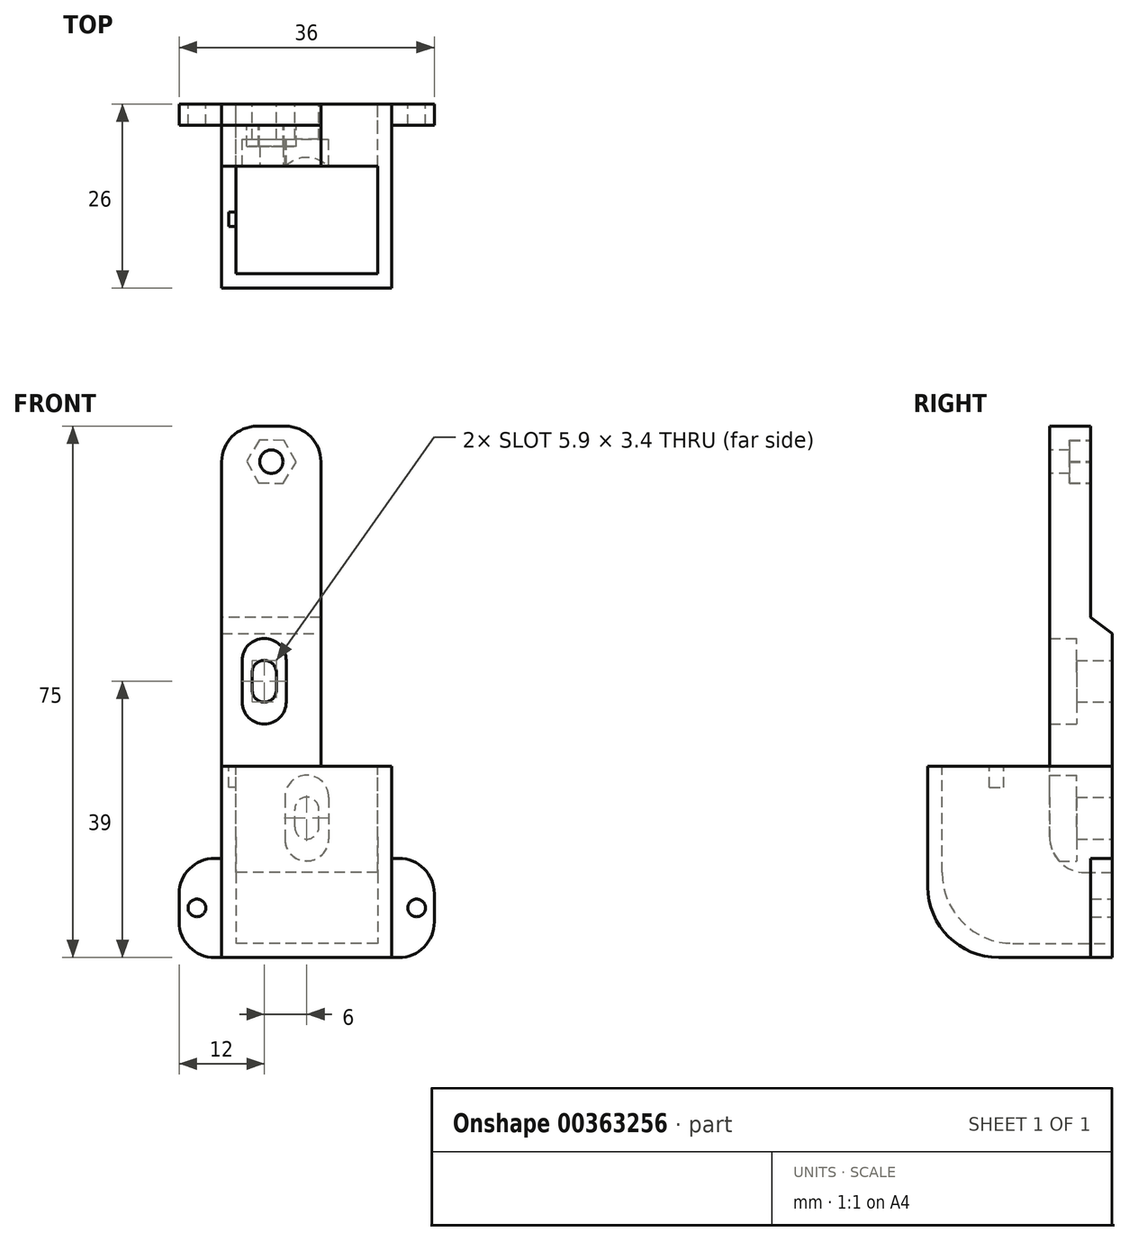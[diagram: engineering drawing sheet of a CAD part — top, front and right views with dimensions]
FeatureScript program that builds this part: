
annotation { "Feature Type Name" : "Feature", "Feature Type Description" : "" }
export const myFeature = defineFeature(function(context is Context, id is Id, definition is map)
    precondition{}
    {
        {
            var Q0;
            Q0=qCreatedBy(makeId("Top.planeOp"),FACE);
            var sketch = newSketch(context, id + "F0", { "sketchPlane" : qUnion([Q0])});
            skLineSegment(sketch, "E0.bottom", {"start": v(12, 13) * mm, "end": v(-12, 13) * mm});
            skLineSegment(sketch, "E0.top", {"start": v(12, -13) * mm, "end": v(-12, -13) * mm});
            skLineSegment(sketch, "E0.left", {"start": v(12, 13) * mm, "end": v(12, -13) * mm});
            skLineSegment(sketch, "E0.right", {"start": v(-12, 13) * mm, "end": v(-12, -13) * mm});
            skPoint(sketch, "E0.middle", {"position": v(0, 0) * mm});
            skSolve(sketch);
        }
        {
            var Q0;
            Q0=qSketchRegion(id+"F0",true);
            extrude(context, id + "F1", {"entities" : qUnion([Q0]), "depth" : 27 * mm});
        }
        {
            var Q0;
            Q0=makeQuery(id+"F1.opExtrude","CAP_FACE",FACE,{"disambiguationData":[OSD([sQuery(id+"F0.wireOp",EDGE,"E0.bottom"),sQuery(id+"F0.wireOp",EDGE,"E0.top"),sQuery(id+"F0.wireOp",EDGE,"E0.left"),sQuery(id+"F0.wireOp",EDGE,"E0.right")])],"isStart":false});
            var sketch = newSketch(context, id + "F2", { "sketchPlane" : qUnion([Q0])});
            skLineSegment(sketch, "E1.bottom", {"start": v(-10, -11) * mm, "end": v(10, -11) * mm});
            skLineSegment(sketch, "E1.top", {"start": v(-10, 4.2) * mm, "end": v(10, 4.2) * mm});
            skLineSegment(sketch, "E1.left", {"start": v(-10, -11) * mm, "end": v(-10, 4.2) * mm});
            skLineSegment(sketch, "E1.right", {"start": v(10, -11) * mm, "end": v(10, 4.2) * mm});
            skSolve(sketch);
        }
        {
            var Q0;
            Q0=qSketchRegion(id+"F2",true);
            extrude(context, id + "F3", {"entities" : qUnion([Q0]), "operationType" : NewBodyOperationType.REMOVE, "oppositeDirection" : true, "depth" : 25 * mm});
        }
        {
            var Q0;
            Q0=makeQuery(id+"F1.opExtrude","SWEPT_FACE",FACE,{"disambiguationData":[OSD([sQuery(id+"F0.wireOp",EDGE,"E0.bottom")])]});
            var sketch = newSketch(context, id + "F4", { "sketchPlane" : qUnion([Q0])});
            skLineSegment(sketch, "E2.bottom", {"start": v(-10, 12) * mm, "end": v(10, 12) * mm});
            skLineSegment(sketch, "E2.top", {"start": v(-10, 2) * mm, "end": v(10, 2) * mm});
            skLineSegment(sketch, "E2.left", {"start": v(-10, 12) * mm, "end": v(-10, 2) * mm});
            skLineSegment(sketch, "E2.right", {"start": v(10, 12) * mm, "end": v(10, 2) * mm});
            skSolve(sketch);
        }
        {
            var Q0;
            Q0=qSketchRegion(id+"F4",true);
            var Q1;
            Q1=makeQuery(id+"F3.boolean.opBoolean","COPY",FACE,{"derivedFrom":makeQuery(id+"F3.opExtrude","SWEPT_FACE",FACE,{"disambiguationData":[OSD([sQuery(id+"F2.wireOp",EDGE,"E1.bottom")])]})});
            extrude(context, id + "F5", {"entities" : qUnion([Q0]), "operationType" : NewBodyOperationType.REMOVE, "endBound" : BoundingType.UP_TO_SURFACE, "oppositeDirection" : true, "endBoundEntityFace" : qUnion([Q1]), "depth" : 25 * mm});
        }
        {
            var Q0;
            Q0=makeQuery(id+"F1.opExtrude","SWEPT_FACE",FACE,{"disambiguationData":[OSD([sQuery(id+"F0.wireOp",EDGE,"E0.right")])]});
            var sketch = newSketch(context, id + "F6", { "sketchPlane" : qUnion([Q0])});
            skLineSegment(sketch, "E3.bottom", {"start": v(-13, 0) * mm, "end": v(-10, 0) * mm});
            skLineSegment(sketch, "E3.top", {"start": v(-13, 14) * mm, "end": v(-10, 14) * mm});
            skLineSegment(sketch, "E3.left", {"start": v(-13, 0) * mm, "end": v(-13, 14) * mm});
            skLineSegment(sketch, "E3.right", {"start": v(-10, 0) * mm, "end": v(-10, 14) * mm});
            skSolve(sketch);
        }
        {
            var Q0;
            Q0=makeQuery(id+"F1.opExtrude","SWEPT_FACE",FACE,{"disambiguationData":[OSD([sQuery(id+"F0.wireOp",EDGE,"E0.left")])]});
            var sketch = newSketch(context, id + "F7", { "sketchPlane" : qUnion([Q0])});
            skLineSegment(sketch, "E4.bottom", {"start": v(13, 0) * mm, "end": v(10, 0) * mm});
            skLineSegment(sketch, "E4.top", {"start": v(13, 14) * mm, "end": v(10, 14) * mm});
            skLineSegment(sketch, "E4.left", {"start": v(13, 0) * mm, "end": v(13, 14) * mm});
            skLineSegment(sketch, "E4.right", {"start": v(10, 0) * mm, "end": v(10, 14) * mm});
            skSolve(sketch);
        }
        {
            var Q0;
            Q0=makeQuery(id+"F7.imprint","IMPRINT",FACE,{"disambiguationData":[TD([[makeQuery(id+"F7.imprint","IMPRINT",EDGE,{"derivedFrom":sQuery(id+"F7.wireOp",EDGE,"E4.bottom")}),-1.0]])]});
            extrude(context, id + "F8", {"entities" : qUnion([Q0]), "operationType" : NewBodyOperationType.ADD, "depth" : 6 * mm});
        }
        {
            var Q0;
            Q0=makeQuery(id+"F6.imprint","IMPRINT",FACE,{"disambiguationData":[TD([[makeQuery(id+"F6.imprint","IMPRINT",EDGE,{"derivedFrom":sQuery(id+"F6.wireOp",EDGE,"E3.bottom")}),1.0]])]});
            extrude(context, id + "F9", {"entities" : qUnion([Q0]), "operationType" : NewBodyOperationType.ADD, "depth" : 6 * mm});
        }
        {
            var Q0;
            Q0=makeQuery(id+"F9.boolean.opBoolean","MERGE",FACE,{"derivedFrom":[makeQuery(id+"F8.boolean.opBoolean","MERGE",FACE,{"derivedFrom":[makeQuery(id+"F1.opExtrude","SWEPT_FACE",FACE,{"disambiguationData":[OSD([sQuery(id+"F0.wireOp",EDGE,"E0.bottom")])]}),makeQuery(id+"F8.opExtrude","SWEPT_FACE",FACE,{"disambiguationData":[OSD([sQuery(id+"F7.wireOp",EDGE,"E4.left")])]})]}),makeQuery(id+"F9.opExtrude","SWEPT_FACE",FACE,{"disambiguationData":[OSD([sQuery(id+"F6.wireOp",EDGE,"E3.left")])]})]});
            var sketch = newSketch(context, id + "F10", { "sketchPlane" : qUnion([Q0])});
            skCircle(sketch, "E5", {"center": v(-15.5, 7) * mm, "radius": 1.25 * mm});
            skCircle(sketch, "E6", {"center": v(15.5, 7) * mm, "radius": 1.25 * mm});
            skSolve(sketch);
        }
        {
            var Q0;
            Q0=qSketchRegion(id+"F10",true);
            extrude(context, id + "F11", {"entities" : qUnion([Q0]), "operationType" : NewBodyOperationType.REMOVE, "endBound" : BoundingType.UP_TO_NEXT, "oppositeDirection" : true, "depth" : 25 * mm});
        }
        {
            var Q0;
            Q0=makeQuery(id+"F8.opExtrude","CAP_EDGE",EDGE,{"disambiguationData":[OSD([sQuery(id+"F7.wireOp",EDGE,"E4.top")])],"isStart":false});
            var Q1;
            Q1=makeQuery(id+"F8.opExtrude","CAP_EDGE",EDGE,{"disambiguationData":[OSD([sQuery(id+"F7.wireOp",EDGE,"E4.bottom")])],"isStart":false});
            var Q2;
            Q2=makeQuery(id+"F9.opExtrude","CAP_EDGE",EDGE,{"disambiguationData":[OSD([sQuery(id+"F6.wireOp",EDGE,"E3.top")])],"isStart":false});
            var Q3;
            Q3=makeQuery(id+"F9.opExtrude","CAP_EDGE",EDGE,{"disambiguationData":[OSD([sQuery(id+"F6.wireOp",EDGE,"E3.bottom")])],"isStart":false});
            fillet(context, id + "F12", {"entities" : qUnion([Q0, Q1, Q2, Q3]), "radius" : 5 * mm, "tangentPropagation" : true, "allowEdgeOverflow" : false});
        }
        {
            var Q0;
            Q0=makeQuery(id+"F1.opExtrude","CAP_FACE",FACE,{"disambiguationData":[OSD([sQuery(id+"F0.wireOp",EDGE,"E0.bottom"),sQuery(id+"F0.wireOp",EDGE,"E0.top"),sQuery(id+"F0.wireOp",EDGE,"E0.left"),sQuery(id+"F0.wireOp",EDGE,"E0.right")])],"isStart":false});
            var sketch = newSketch(context, id + "F13", { "sketchPlane" : qUnion([Q0])});
            skLineSegment(sketch, "E7.bottom", {"start": v(-12, 13) * mm, "end": v(2, 13) * mm});
            skLineSegment(sketch, "E7.top", {"start": v(-12, 4.2) * mm, "end": v(2, 4.2) * mm});
            skLineSegment(sketch, "E7.left", {"start": v(-12, 13) * mm, "end": v(-12, 4.2) * mm});
            skLineSegment(sketch, "E7.right", {"start": v(2, 13) * mm, "end": v(2, 4.2) * mm});
            skSolve(sketch);
        }
        {
            var Q0;
            Q0=makeQuery(id+"F13.imprint","IMPRINT",FACE,{"disambiguationData":[TD([[makeQuery(id+"F13.imprint","IMPRINT",EDGE,{"derivedFrom":sQuery(id+"F13.wireOp",EDGE,"E7.bottom")}),1.0]])]});
            extrude(context, id + "F14", {"entities" : qUnion([Q0]), "operationType" : NewBodyOperationType.ADD, "depth" : 48 * mm});
        }
        {
            var Q0;
            Q0=makeQuery(id+"F14.boolean.opBoolean","MERGE",FACE,{"derivedFrom":[makeQuery(id+"F1.opExtrude","SWEPT_FACE",FACE,{"disambiguationData":[OSD([sQuery(id+"F0.wireOp",EDGE,"E0.right")])]}),makeQuery(id+"F14.opExtrude","SWEPT_FACE",FACE,{"disambiguationData":[OSD([sQuery(id+"F13.wireOp",EDGE,"E7.left")])]})]});
            var sketch = newSketch(context, id + "F15", { "sketchPlane" : qUnion([Q0])});
            skLineSegment(sketch, "E8.bottom", {"start": v(-13, 75) * mm, "end": v(-10, 75) * mm});
            skLineSegment(sketch, "E8.top", {"start": v(-13, 45) * mm, "end": v(-10, 45) * mm});
            skLineSegment(sketch, "E8.left", {"start": v(-13, 75) * mm, "end": v(-13, 45) * mm});
            skLineSegment(sketch, "E8.right", {"start": v(-10, 75) * mm, "end": v(-10, 45) * mm});
            skLineSegment(sketch, "E9", {"start": v(-13, 18) * mm, "end": v(-7.21, 18) * mm, "construction": true});
            skSolve(sketch);
        }
        {
            var Q0;
            Q0=qSketchRegion(id+"F15",true);
            extrude(context, id + "F16", {"entities" : qUnion([Q0]), "operationType" : NewBodyOperationType.REMOVE, "endBound" : BoundingType.UP_TO_NEXT, "oppositeDirection" : true, "depth" : 25 * mm});
        }
        {
            var Q0;
            Q0=makeQuery(id+"F16.boolean.opBoolean","COPY",EDGE,{"derivedFrom":makeQuery(id+"F16.opExtrude","SWEPT_EDGE",EDGE,{"disambiguationData":[OSD([sQuery(id+"F15.wireOp",EDGE,"E8.top"),sQuery(id+"F15.wireOp",EDGE,"E8.right")])]})});
            chamfer(context, id + "F17", {"entities" : qUnion([Q0]), "chamferType" : ChamferType.TWO_OFFSETS, "width1" : 3 * mm, "oppositeDirection" : false, "width2" : 4 * mm, "tangentPropagation" : true});
        }
        {
            var Q0;
            Q0=makeQuery(id+"F14.boolean.opBoolean","MERGE",FACE,{"derivedFrom":[makeQuery(id+"F3.boolean.opBoolean","COPY",FACE,{"derivedFrom":makeQuery(id+"F3.opExtrude","SWEPT_FACE",FACE,{"disambiguationData":[OSD([sQuery(id+"F2.wireOp",EDGE,"E1.top")])]})}),makeQuery(id+"F14.opExtrude","SWEPT_FACE",FACE,{"disambiguationData":[OSD([sQuery(id+"F13.wireOp",EDGE,"E7.top")])]})]});
            var sketch = newSketch(context, id + "F18", { "sketchPlane" : qUnion([Q0])});
            skCircle(sketch, "E10", {"center": v(-5, 70) * mm, "radius": 1.65 * mm});
            skSolve(sketch);
        }
        {
            var Q0;
            Q0=qSketchRegion(id+"F18",true);
            extrude(context, id + "F19", {"entities" : qUnion([Q0]), "operationType" : NewBodyOperationType.REMOVE, "endBound" : BoundingType.UP_TO_NEXT, "oppositeDirection" : true, "depth" : 25 * mm});
        }
        {
            var Q0;
            Q0=makeQuery(id+"F16.boolean.opBoolean","COPY",FACE,{"derivedFrom":makeQuery(id+"F16.opExtrude","SWEPT_FACE",FACE,{"disambiguationData":[OSD([sQuery(id+"F15.wireOp",EDGE,"E8.right")])]})});
            var sketch = newSketch(context, id + "F20", { "sketchPlane" : qUnion([Q0])});
            skCircle(sketch, "E11.cCircle", {"center": v(5, 70) * mm, "radius": 3.5 * mm, "construction": true});
            skLineSegment(sketch, "E11.0", {"start": v(6.7, 73.06) * mm, "end": v(8.5, 70.06) * mm});
            skLineSegment(sketch, "E11.1", {"start": v(8.5, 70.06) * mm, "end": v(6.8, 67) * mm});
            skLineSegment(sketch, "E11.2", {"start": v(6.8, 67) * mm, "end": v(3.3, 66.94) * mm});
            skLineSegment(sketch, "E11.3", {"start": v(3.3, 66.94) * mm, "end": v(1.5, 69.94) * mm});
            skLineSegment(sketch, "E11.4", {"start": v(1.5, 69.94) * mm, "end": v(3.2, 73) * mm});
            skLineSegment(sketch, "E11.5", {"start": v(3.2, 73) * mm, "end": v(6.7, 73.06) * mm});
            skSolve(sketch);
        }
        {
            var Q0;
            Q0=qSketchRegion(id+"F20",true);
            extrude(context, id + "F21", {"entities" : qUnion([Q0]), "operationType" : NewBodyOperationType.REMOVE, "oppositeDirection" : true, "depth" : 3 * mm});
        }
        {
            var Q0;
            Q0=makeQuery(id+"F14.boolean.opBoolean","MERGE",FACE,{"derivedFrom":[makeQuery(id+"F9.boolean.opBoolean","MERGE",FACE,{"derivedFrom":[makeQuery(id+"F8.boolean.opBoolean","MERGE",FACE,{"derivedFrom":[makeQuery(id+"F1.opExtrude","SWEPT_FACE",FACE,{"disambiguationData":[OSD([sQuery(id+"F0.wireOp",EDGE,"E0.bottom")])]}),makeQuery(id+"F8.opExtrude","SWEPT_FACE",FACE,{"disambiguationData":[OSD([sQuery(id+"F7.wireOp",EDGE,"E4.left")])]})]}),makeQuery(id+"F9.opExtrude","SWEPT_FACE",FACE,{"disambiguationData":[OSD([sQuery(id+"F6.wireOp",EDGE,"E3.left")])]})]}),makeQuery(id+"F14.opExtrude","SWEPT_FACE",FACE,{"disambiguationData":[OSD([sQuery(id+"F13.wireOp",EDGE,"E7.bottom")])]})]});
            var sketch = newSketch(context, id + "F22", { "sketchPlane" : qUnion([Q0])});
            skLineSegment(sketch, "E12", {"start": v(-12, 18) * mm, "end": v(12, 18) * mm, "construction": true});
            skLineSegment(sketch, "E13", {"start": v(0, 18) * mm, "end": v(0, 19.67) * mm, "construction": true});
            skLineSegment(sketch, "E14", {"start": v(0, 18.42) * mm, "end": v(0, 20.93) * mm, "construction": true});
            skPoint(sketch, "E15", {"position": v(0, 19.67) * mm});
            skArc(sketch, "E16.0.startCap", {"start": v(1.7, 18.42) * mm, "mid": v(0, 16.72) * mm, "end": v(-1.7, 18.42) * mm});
            skArc(sketch, "E16.0.endCap", {"start": v(-1.7, 20.92) * mm, "mid": v(0, 22.62) * mm, "end": v(1.7, 20.92) * mm});
            skLineSegment(sketch, "E16.0.left", {"start": v(-1.7, 18.42) * mm, "end": v(-1.7, 20.92) * mm});
            skLineSegment(sketch, "E16.0.right", {"start": v(1.7, 18.42) * mm, "end": v(1.7, 20.92) * mm});
            skLineSegment(sketch, "E17", {"start": v(0, 22.62) * mm, "end": v(0, 16.72) * mm});
            skArc(sketch, "E18.0.startCap", {"start": v(-3.1, 22.62) * mm, "mid": v(0, 25.72) * mm, "end": v(3.1, 22.62) * mm});
            skArc(sketch, "E18.0.endCap", {"start": v(3.1, 16.72) * mm, "mid": v(0, 13.62) * mm, "end": v(-3.1, 16.72) * mm});
            skLineSegment(sketch, "E18.0.left", {"start": v(3.1, 22.62) * mm, "end": v(3.1, 16.72) * mm});
            skLineSegment(sketch, "E18.0.right", {"start": v(-3.1, 22.62) * mm, "end": v(-3.1, 16.72) * mm});
            skLineSegment(sketch, "E19", {"start": v(6, 40.25) * mm, "end": v(6, 37.75) * mm});
            skPoint(sketch, "E20", {"position": v(6, 39) * mm});
            skArc(sketch, "E21.0.startCap", {"start": v(4.3, 40.25) * mm, "mid": v(6, 41.95) * mm, "end": v(7.7, 40.25) * mm});
            skArc(sketch, "E21.0.endCap", {"start": v(7.7, 37.75) * mm, "mid": v(6, 36.05) * mm, "end": v(4.3, 37.75) * mm});
            skLineSegment(sketch, "E21.0.left", {"start": v(7.7, 40.25) * mm, "end": v(7.7, 37.75) * mm});
            skLineSegment(sketch, "E21.0.right", {"start": v(4.3, 40.25) * mm, "end": v(4.3, 37.75) * mm});
            skLineSegment(sketch, "E22", {"start": v(6, 41.95) * mm, "end": v(6, 36.05) * mm});
            skArc(sketch, "E23.0.startCap", {"start": v(2.9, 41.95) * mm, "mid": v(6, 45.05) * mm, "end": v(9.1, 41.95) * mm});
            skArc(sketch, "E23.0.endCap", {"start": v(9.1, 36.05) * mm, "mid": v(6, 32.95) * mm, "end": v(2.9, 36.05) * mm});
            skLineSegment(sketch, "E23.0.left", {"start": v(9.1, 41.95) * mm, "end": v(9.1, 36.05) * mm});
            skLineSegment(sketch, "E23.0.right", {"start": v(2.9, 41.95) * mm, "end": v(2.9, 36.05) * mm});
            skSolve(sketch);
        }
        {
            var Q0;
            Q0=qSketchRegion(id+"F22",true);
            var Q1;
            {var subQ0=sQuery(id+"F22.wireOp",EDGE,"E16.0.left");Q1=makeQuery(id+"F22.imprint","IMPRINT",FACE,{"disambiguationData":[TD([[makeQuery(id+"F22.imprint","IMPRINT",EDGE,{"derivedFrom":subQ0}),-1.0]])]});}
            var Q2;
            {var subQ0=sQuery(id+"F22.wireOp",EDGE,"E16.0.right");Q2=makeQuery(id+"F22.imprint","IMPRINT",FACE,{"disambiguationData":[TD([[makeQuery(id+"F22.imprint","IMPRINT",EDGE,{"derivedFrom":subQ0}),1.0]])]});}
            var Q3;
            {var subQ0=sQuery(id+"F22.wireOp",EDGE,"E21.0.left");Q3=makeQuery(id+"F22.imprint","IMPRINT",FACE,{"disambiguationData":[TD([[makeQuery(id+"F22.imprint","IMPRINT",EDGE,{"derivedFrom":subQ0}),-1.0]])]});}
            var Q4;
            {var subQ4=sQuery(id+"F22.wireOp",EDGE,"E21.0.right");Q4=makeQuery(id+"F22.imprint","IMPRINT",FACE,{"disambiguationData":[TD([[makeQuery(id+"F22.imprint","IMPRINT",EDGE,{"derivedFrom":subQ4}),1.0]])]});}
            extrude(context, id + "F23", {"entities" : qUnion([Q0, Q1, Q2, Q3, Q4]), "operationType" : NewBodyOperationType.REMOVE, "endBound" : BoundingType.UP_TO_NEXT, "oppositeDirection" : true, "depth" : 25 * mm});
        }
        {
            var Q0;
            Q0=qSketchRegion(id+"F22",true);
            extrude(context, id + "F24", {"entities" : qUnion([Q0]), "operationType" : NewBodyOperationType.ADD, "oppositeDirection" : true, "depth" : 5 * mm});
        }
        {
            var Q0;
            Q0=makeQuery(id+"F1.opExtrude","CAP_EDGE",EDGE,{"disambiguationData":[OSD([sQuery(id+"F0.wireOp",EDGE,"E0.top")])],"isStart":true});
            var Q1;
            Q1=makeQuery(id+"F3.boolean.opBoolean","COPY",EDGE,{"derivedFrom":makeQuery(id+"F3.opExtrude","CAP_EDGE",EDGE,{"disambiguationData":[OSD([sQuery(id+"F2.wireOp",EDGE,"E1.bottom")])],"isStart":false})});
            fillet(context, id + "F25", {"entities" : qUnion([Q0, Q1]), "radius" : 10 * mm, "tangentPropagation" : true, "allowEdgeOverflow" : false});
        }
        {
            var Q0;
            Q0=makeQuery(id+"F5.boolean.opBoolean","INTERSECT",EDGE,{"derivedFrom":[makeQuery(id+"F3.boolean.opBoolean","COPY",FACE,{"derivedFrom":makeQuery(id+"F3.opExtrude","SWEPT_FACE",FACE,{"disambiguationData":[OSD([sQuery(id+"F2.wireOp",EDGE,"E1.top")])]})}),makeQuery(id+"F5.opExtrude","SWEPT_FACE",FACE,{"disambiguationData":[OSD([sQuery(id+"F4.wireOp",EDGE,"E2.bottom")])]})]});
            fillet(context, id + "F26", {"entities" : qUnion([Q0]), "radius" : 5 * mm, "tangentPropagation" : true, "allowEdgeOverflow" : false});
        }
        {
            var Q0;
            Q0=makeQuery(id+"F1.opExtrude","CAP_FACE",FACE,{"disambiguationData":[OSD([sQuery(id+"F0.wireOp",EDGE,"E0.bottom"),sQuery(id+"F0.wireOp",EDGE,"E0.top"),sQuery(id+"F0.wireOp",EDGE,"E0.left"),sQuery(id+"F0.wireOp",EDGE,"E0.right")])],"isStart":false});
            var sketch = newSketch(context, id + "F27", { "sketchPlane" : qUnion([Q0])});
            skLineSegment(sketch, "E24.bottom", {"start": v(-10, -4.3) * mm, "end": v(-11, -4.3) * mm});
            skLineSegment(sketch, "E24.top", {"start": v(-10, -2.3) * mm, "end": v(-11, -2.3) * mm});
            skLineSegment(sketch, "E24.left", {"start": v(-10, -4.3) * mm, "end": v(-10, -2.3) * mm});
            skLineSegment(sketch, "E24.right", {"start": v(-11, -4.3) * mm, "end": v(-11, -2.3) * mm});
            skSolve(sketch);
        }
        {
            var Q0;
            Q0=makeQuery(id+"F27.imprint","IMPRINT",FACE,{"disambiguationData":[TD([[makeQuery(id+"F27.imprint","IMPRINT",EDGE,{"derivedFrom":sQuery(id+"F27.wireOp",EDGE,"E24.bottom")}),-1.0]])]});
            extrude(context, id + "F28", {"entities" : qUnion([Q0]), "operationType" : NewBodyOperationType.REMOVE, "oppositeDirection" : true, "depth" : 3 * mm});
        }
        {
            var Q0;
            Q0=makeQuery(id+"F14.opExtrude","CAP_EDGE",EDGE,{"disambiguationData":[OSD([sQuery(id+"F13.wireOp",EDGE,"E7.left")])],"isStart":false});
            var Q1;
            Q1=makeQuery(id+"F14.opExtrude","CAP_EDGE",EDGE,{"disambiguationData":[OSD([sQuery(id+"F13.wireOp",EDGE,"E7.right")])],"isStart":false});
            fillet(context, id + "F29", {"entities" : qUnion([Q0, Q1]), "radius" : 5 * mm, "tangentPropagation" : true, "allowEdgeOverflow" : false});
        }
    });
